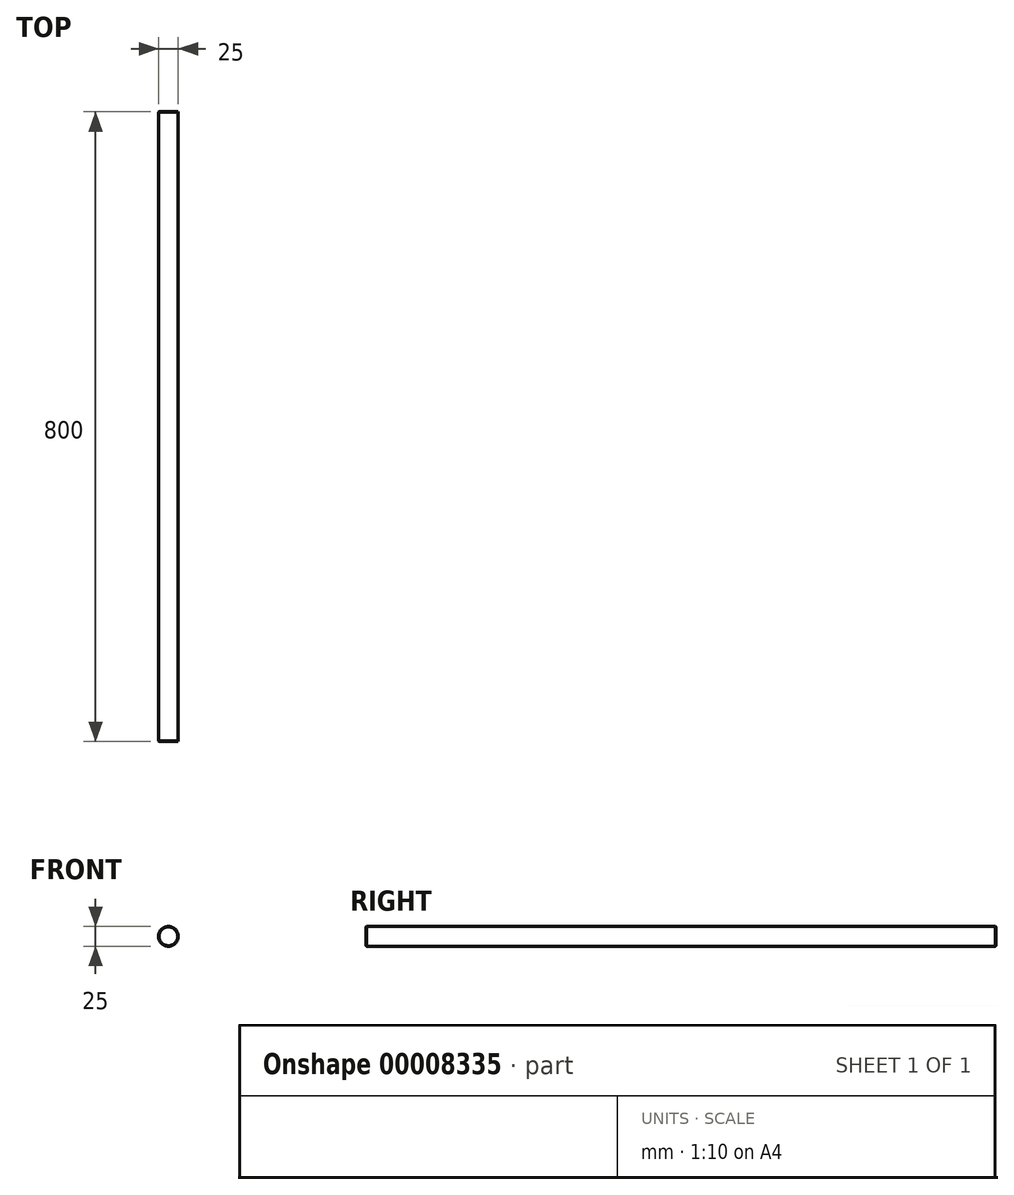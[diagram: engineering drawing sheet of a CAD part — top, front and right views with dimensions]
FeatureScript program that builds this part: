
annotation { "Feature Type Name" : "Feature", "Feature Type Description" : "" }
export const myFeature = defineFeature(function(context is Context, id is Id, definition is map)
    precondition{}
    {
        {
            var Q0;
            Q0=qCreatedBy(makeId("Front.planeOp"),FACE);
            var sketch = newSketch(context, id + "F0", { "sketchPlane" : qUnion([Q0])});
            skCircle(sketch, "E0", {"center": v(0, 0) * mm, "radius": 12.5 * mm});
            skSolve(sketch);
        }
        {
            var Q0;
            Q0 = qSketchRegion(id + "F0", true);
            extrude(context, id + "F1", {"entities" : qUnion([Q0]), "depth" : 800 * mm});
        }
        {
            var Q0;
            Q0=makeQuery(id+"F1.opExtrude","CAP_EDGE",EDGE,{"disambiguationData":[OSD([sQuery(id+"F0.wireOp",EDGE,"E0")])],"isStart":false});
            var Q1;
            Q1=makeQuery(id+"F1.opExtrude","CAP_EDGE",EDGE,{"disambiguationData":[OSD([sQuery(id+"F0.wireOp",EDGE,"E0")])],"isStart":true});
            chamfer(context, id + "F2", {"entities" : qUnion([Q0, Q1]), "width" : 0.5 * mm, "tangentPropagation" : true});
        }
    });
